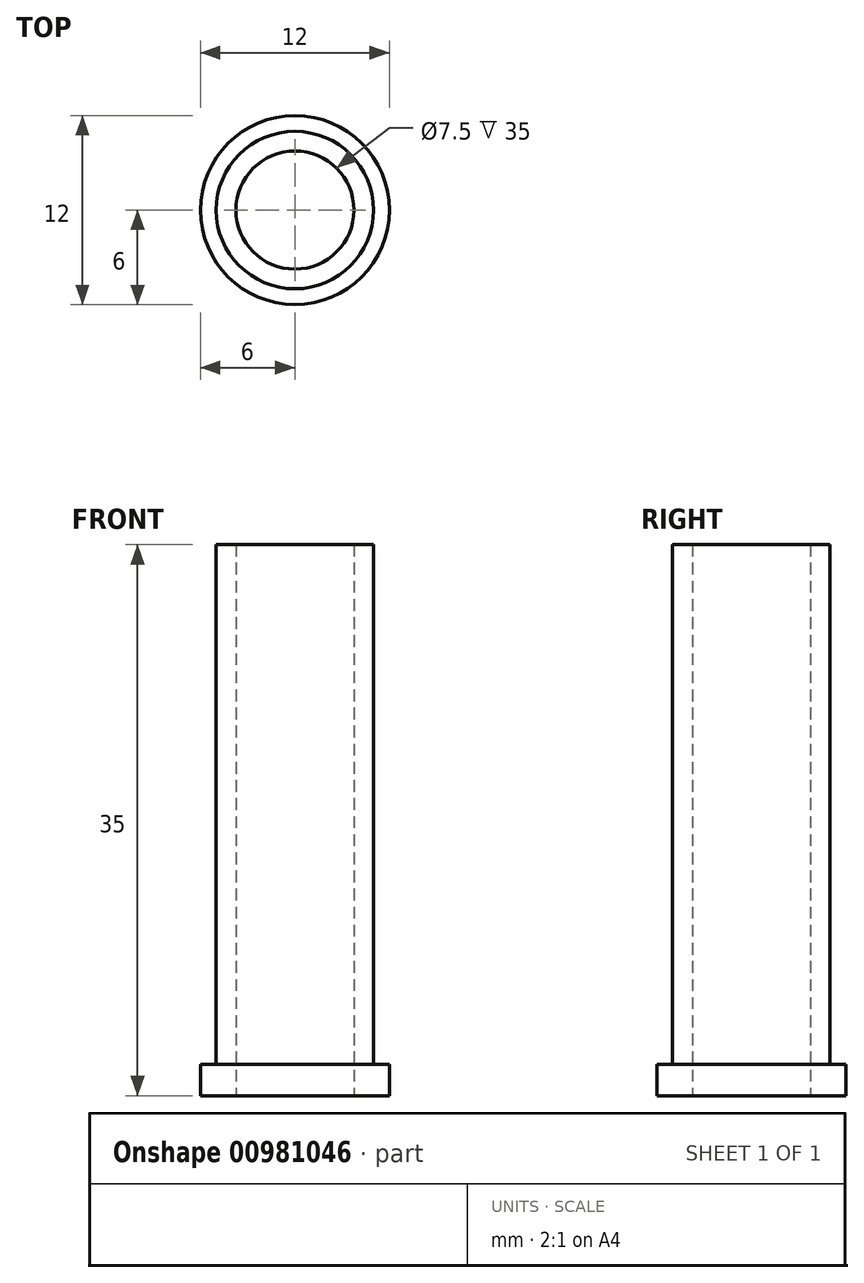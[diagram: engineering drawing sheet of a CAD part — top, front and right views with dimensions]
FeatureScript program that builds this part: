
annotation { "Feature Type Name" : "Feature", "Feature Type Description" : "" }
export const myFeature = defineFeature(function(context is Context, id is Id, definition is map)
    precondition{}
    {
        {
            var Q0;
            Q0=qCreatedBy(makeId("Top.planeOp"),FACE);
            var sketch = newSketch(context, id + "F0", { "sketchPlane" : qUnion([Q0])});
            skCircle(sketch, "E0", {"center": v(0, 0) * mm, "radius": 5 * mm});
            skSolve(sketch);
        }
        {
            var Q0;
            Q0=makeQuery(id+"F0.imprint","IMPRINT",FACE,{"disambiguationData":[TD([[makeQuery(id+"F0.imprint","IMPRINT",EDGE,{"derivedFrom":sQuery(id+"F0.wireOp",EDGE,"E0")}),1.0]])]});
            extrude(context, id + "F1", {"entities" : qUnion([Q0]), "depth" : 33 * mm, "offsetDistance" : 25 * mm});
        }
        {
            var Q0;
            Q0=makeQuery(id+"F1.opExtrude","CAP_FACE",FACE,{"disambiguationData":[OSD([sQuery(id+"F0.wireOp",EDGE,"E0")])],"isStart":true});
            var Q1;
            Q1=makeQuery(id+"F1.opExtrude","CAP_FACE",FACE,{"disambiguationData":[OSD([sQuery(id+"F0.wireOp",EDGE,"E0")])],"isStart":true});
            var sketch = newSketch(context, id + "F2", { "sketchPlane" : qUnion([Q0, Q1])});
            skCircle(sketch, "E1", {"center": v(0, 0) * mm, "radius": 6 * mm});
            skSolve(sketch);
        }
        {
            var Q0;
            Q0 = qSketchRegion(id + "F2", true);
            extrude(context, id + "F3", {"entities" : qUnion([Q0]), "operationType" : NewBodyOperationType.ADD, "depth" : 2 * mm, "offsetDistance" : 25 * mm});
        }
        {
            var Q0;
            Q0=makeQuery(id+"F3.opExtrude","CAP_FACE",FACE,{"disambiguationData":[OSD([sQuery(id+"F2.wireOp",EDGE,"E1")])],"isStart":false});
            var Q1;
            Q1=makeQuery(id+"F3.opExtrude","CAP_FACE",FACE,{"disambiguationData":[OSD([sQuery(id+"F2.wireOp",EDGE,"E1")])],"isStart":false});
            var sketch = newSketch(context, id + "F4", { "sketchPlane" : qUnion([Q0, Q1])});
            skCircle(sketch, "E2", {"center": v(0, 0) * mm, "radius": 3.75 * mm});
            skSolve(sketch);
        }
        {
            var Q0;
            Q0 = qSketchRegion(id + "F4", true);
            extrude(context, id + "F5", {"entities" : qUnion([Q0]), "operationType" : NewBodyOperationType.REMOVE, "endBound" : BoundingType.THROUGH_ALL, "oppositeDirection" : true, "depth" : 25 * mm, "offsetDistance" : 25 * mm});
        }
    });
